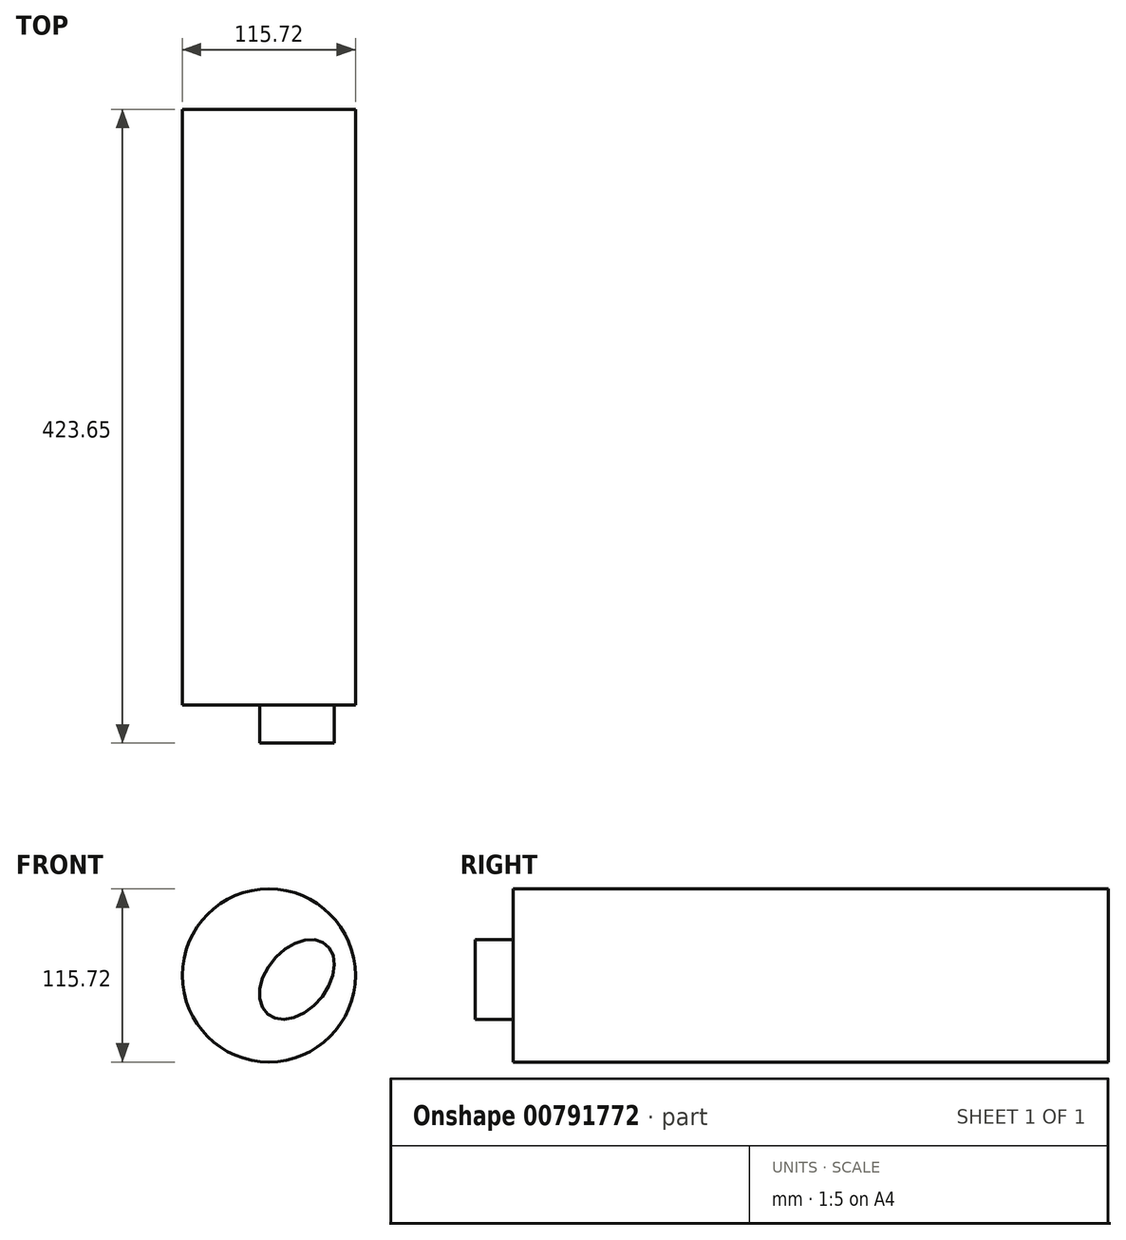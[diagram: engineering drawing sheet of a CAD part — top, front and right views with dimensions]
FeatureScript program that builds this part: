
annotation { "Feature Type Name" : "Feature", "Feature Type Description" : "" }
export const myFeature = defineFeature(function(context is Context, id is Id, definition is map)
    precondition{}
    {
        {
            var Q0;
            Q0=qCreatedBy(makeId("Front.planeOp"),FACE);
            var sketch = newSketch(context, id + "F0", { "sketchPlane" : qUnion([Q0])});
            skCircle(sketch, "E0", {"center": v(70.25, 58.85) * mm, "radius": 57.86 * mm});
            skSolve(sketch);
        }
        {
            var Q0;
            Q0=makeQuery(id+"F0.imprint","IMPRINT",FACE,{"disambiguationData":[TD([[makeQuery(id+"F0.imprint","IMPRINT",EDGE,{"derivedFrom":sQuery(id+"F0.wireOp",EDGE,"E0")}),1.0]])]});
            extrude(context, id + "F1", {"entities" : qUnion([Q0]), "depth" : 253.4 * mm, "offsetDistance" : 25.4 * mm});
        }
        {
            var Q0;
            Q0=makeQuery(id+"F1.opExtrude","CAP_FACE",FACE,{"disambiguationData":[OSD([sQuery(id+"F0.wireOp",EDGE,"E0")])],"isStart":false});
            extrude(context, id + "F2", {"entities" : qUnion([Q0]), "operationType" : NewBodyOperationType.ADD, "depth" : 144.84 * mm, "offsetDistance" : 25.4 * mm});
        }
        {
            var Q0;
            Q0=makeQuery(id+"F2.opExtrude","CAP_FACE",FACE,{"disambiguationData":[OSD([sQuery(id+"F0.wireOp",EDGE,"E0")])],"isStart":false});
            var sketch = newSketch(context, id + "F3", { "sketchPlane" : qUnion([Q0])});
            skSolve(sketch);
        }
        {
            var Q0;
            Q0=makeQuery(id+"F3.imprint","IMPRINT",FACE,{"disambiguationData":[TD([[makeQuery(id+"F3.imprint","IMPRINT",EDGE,{"derivedFrom":makeQuery(id+"F2.opExtrude","CAP_EDGE",EDGE,{"disambiguationData":[OSD([sQuery(id+"F0.wireOp",EDGE,"E0")])],"isStart":false})}),1.0]])]});
            var sketch = newSketch(context, id + "F4", { "sketchPlane" : qUnion([Q0])});
            skEllipse(sketch, "E1", {"center": v(89.04, 56.24) * mm, "majorRadius": 30.39 * mm, "minorRadius": 20.43 * mm, "majorAxis": v(-0.65, -0.76)});
            skSolve(sketch);
        }
        {
            var Q0;
            Q0=makeQuery(id+"F4.imprint","IMPRINT",FACE,{"disambiguationData":[TD([[makeQuery(id+"F4.imprint","IMPRINT",EDGE,{"derivedFrom":sQuery(id+"F4.wireOp",EDGE,"E1")}),1.0]])]});
            var Q1;
            Q1 = qSketchRegion(id + "F4", true);
            extrude(context, id + "F5", {"entities" : qUnion([Q0, Q1]), "operationType" : NewBodyOperationType.ADD, "depth" : 25.4 * mm, "offsetDistance" : 25.4 * mm});
        }
    });
